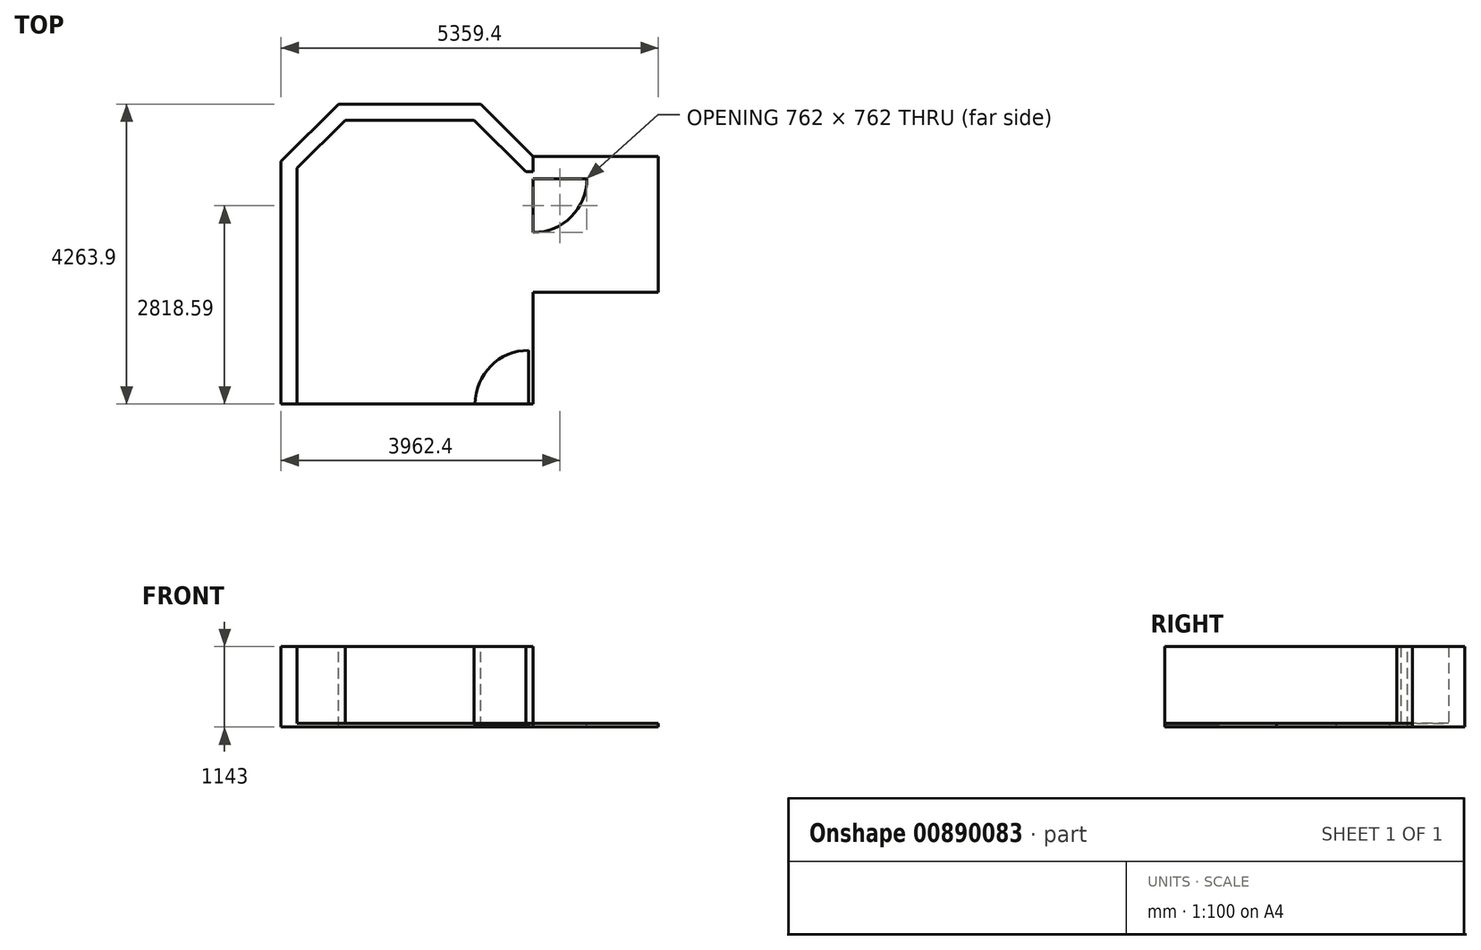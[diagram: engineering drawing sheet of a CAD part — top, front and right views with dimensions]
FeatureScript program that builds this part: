
annotation { "Feature Type Name" : "Feature", "Feature Type Description" : "" }
export const myFeature = defineFeature(function(context is Context, id is Id, definition is map)
    precondition{}
    {
        {
            var Q0;
            Q0=qCreatedBy(makeId("Top.planeOp"),FACE);
            var sketch = newSketch(context, id + "F0", { "sketchPlane" : qUnion([Q0])});
            skLineSegment(sketch, "E0", {"start": v(0, 0) * mm, "end": v(-3581.4, 0) * mm});
            skLineSegment(sketch, "E1", {"start": v(-3581.4, 0) * mm, "end": v(-3581.4, 3447.49) * mm});
            skLineSegment(sketch, "E2", {"start": v(-3581.4, 3447.49) * mm, "end": v(-2764.99, 4263.9) * mm});
            skLineSegment(sketch, "E3", {"start": v(-2764.99, 4263.9) * mm, "end": v(-746.81, 4263.9) * mm});
            skLineSegment(sketch, "E4", {"start": v(-746.81, 4263.9) * mm, "end": v(0, 3517.09) * mm});
            skLineSegment(sketch, "E5", {"start": v(0, 3517.09) * mm, "end": v(0, 0) * mm});
            skLineSegment(sketch, "E6", {"start": v(-3352.8, 0) * mm, "end": v(-3352.8, 3352.8) * mm});
            skLineSegment(sketch, "E7", {"start": v(-3352.8, 3352.8) * mm, "end": v(-2670.3, 4035.3) * mm});
            skLineSegment(sketch, "E8", {"start": v(-2670.3, 4035.3) * mm, "end": v(-841.5, 4035.3) * mm});
            skLineSegment(sketch, "E9", {"start": v(-841.5, 4035.3) * mm, "end": v(-105.12, 3298.92) * mm});
            skLineSegment(sketch, "E10", {"start": v(-105.12, 3298.92) * mm, "end": v(0, 3298.92) * mm});
            skLineSegment(sketch, "E11.bottom", {"start": v(0, 3517.09) * mm, "end": v(1778, 3517.09) * mm});
            skLineSegment(sketch, "E11.top", {"start": v(0, 1586.69) * mm, "end": v(1778, 1586.69) * mm});
            skLineSegment(sketch, "E11.left", {"start": v(0, 3517.09) * mm, "end": v(0, 1586.69) * mm});
            skLineSegment(sketch, "E11.right", {"start": v(1778, 3517.09) * mm, "end": v(1778, 1586.69) * mm});
            skArc(sketch, "E12", {"start": v(762, 3199.59) * mm, "mid": v(538.82, 2660.77) * mm, "end": v(0, 2437.59) * mm});
            skLineSegment(sketch, "E13", {"start": v(0, 3199.59) * mm, "end": v(762, 3199.59) * mm});
            skArc(sketch, "E14", {"start": v(-825.5, 0) * mm, "mid": v(-602.32, 538.82) * mm, "end": v(-63.5, 762) * mm});
            skLineSegment(sketch, "E15", {"start": v(-63.5, 0) * mm, "end": v(-63.5, 762) * mm});
            skSolve(sketch);
        }
        {
            var Q0;
            Q0 = qSketchRegion(id + "F0", true);
            var Q1;
            {var subQ0=sQuery(id+"F0.wireOp",EDGE,"E12");Q1=makeQuery(id+"F0.imprint","IMPRINT",FACE,{"disambiguationData":[TD([[makeQuery(id+"F0.imprint","IMPRINT",EDGE,{"derivedFrom":subQ0}),-1.0]])]});}
            extrude(context, id + "F1", {"entities" : qUnion([Q0, Q1]), "oppositeDirection" : true, "depth" : 25.4 * mm, "offsetDistance" : 25.4 * mm});
        }
        {
            var Q0;
            {var subQ0=sQuery(id+"F0.wireOp",EDGE,"E12");Q0=makeQuery(id+"F0.imprint","IMPRINT",FACE,{"disambiguationData":[TD([[makeQuery(id+"F0.imprint","IMPRINT",EDGE,{"derivedFrom":subQ0}),-1.0]])]});}
            var Q1;
            {var subQ0=sQuery(id+"F0.wireOp",EDGE,"E14");Q1=makeQuery(id+"F0.imprint","IMPRINT",FACE,{"disambiguationData":[TD([[makeQuery(id+"F0.imprint","IMPRINT",EDGE,{"derivedFrom":subQ0}),-1.0]])]});}
            extrude(context, id + "F2", {"entities" : qUnion([Q0, Q1]), "operationType" : NewBodyOperationType.ADD, "depth" : 25.4 * mm, "offsetDistance" : 25.4 * mm});
        }
        {
            var Q0;
            {var subQ3=sQuery(id+"F0.wireOp",EDGE,"E1");Q0=makeQuery(id+"F0.imprint","IMPRINT",FACE,{"disambiguationData":[TD([[makeQuery(id+"F0.imprint","IMPRINT",EDGE,{"derivedFrom":subQ3}),-1.0]])]});}
            extrude(context, id + "F3", {"entities" : qUnion([Q0]), "operationType" : NewBodyOperationType.ADD, "depth" : 1117.6 * mm, "offsetDistance" : 25.4 * mm});
        }
        {
            var Q0;
            Q0=sQuery(id+"F0.wireOp",EDGE,"E0");
            var Q1;
            Q1=sQuery(id+"F0.wireOp",EDGE,"E5");
            var Q2;
            Q2=sQuery(id+"F0.wireOp",EDGE,"E1");
            var Q3;
            Q3=sQuery(id+"F0.wireOp",EDGE,"E2");
            var Q4;
            Q4=sQuery(id+"F0.wireOp",EDGE,"E3");
            var Q5;
            Q5=sQuery(id+"F0.wireOp",EDGE,"E4");
            extrude(context, id + "F4", {"bodyType" : ToolBodyType.SURFACE, "surfaceEntities" : qUnion([Q0, Q1, Q2, Q3, Q4, Q5]), "depth" : 2438.4 * mm, "offsetDistance" : 25.4 * mm});
        }
    });
